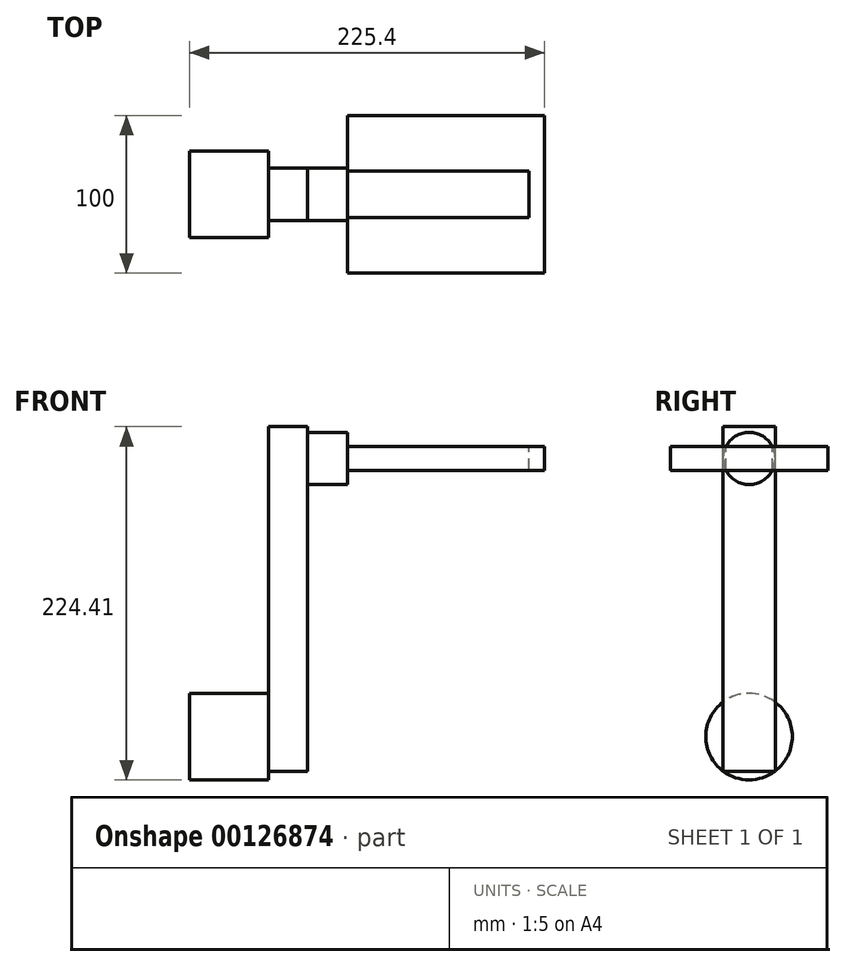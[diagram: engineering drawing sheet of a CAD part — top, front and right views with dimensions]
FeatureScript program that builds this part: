
annotation { "Feature Type Name" : "Feature", "Feature Type Description" : "" }
export const myFeature = defineFeature(function(context is Context, id is Id, definition is map)
    precondition{}
    {
        {
            var Q0;
            Q0=qCreatedBy(makeId("Right.planeOp"),FACE);
            var sketch = newSketch(context, id + "F0", { "sketchPlane" : qUnion([Q0])});
            skCircle(sketch, "E0", {"center": v(-5.47, 22.01) * mm, "radius": 27.5 * mm});
            skSolve(sketch);
        }
        {
            var Q0;
            Q0=makeQuery(id+"F0.imprint","IMPRINT",FACE,{"disambiguationData":[TD([[makeQuery(id+"F0.imprint","IMPRINT",EDGE,{"derivedFrom":sQuery(id+"F0.wireOp",EDGE,"E0")}),1.0]])]});
            extrude(context, id + "F1", {"entities" : qUnion([Q0]), "depth" : 50 * mm});
        }
        {
            var Q0;
            Q0=makeQuery(id+"F1.opExtrude","CAP_FACE",FACE,{"disambiguationData":[OSD([sQuery(id+"F0.wireOp",EDGE,"E0")])],"isStart":false});
            var sketch = newSketch(context, id + "F2", { "sketchPlane" : qUnion([Q0])});
            skLineSegment(sketch, "E1.bottom", {"start": v(-21.95, 0) * mm, "end": v(11.16, 0) * mm});
            skLineSegment(sketch, "E1.top", {"start": v(-21.95, 43.92) * mm, "end": v(11.16, 43.92) * mm});
            skLineSegment(sketch, "E1.left", {"start": v(-21.95, 0) * mm, "end": v(-21.95, 43.92) * mm});
            skLineSegment(sketch, "E1.right", {"start": v(11.16, 0) * mm, "end": v(11.16, 43.92) * mm});
            skSolve(sketch);
        }
        {
            var Q0;
            {var subQ0=sQuery(id+"F2.wireOp",EDGE,"E1.right");var subQ1=sQuery(id+"F2.wireOp",EDGE,"E1.bottom");var subQ2=makeQuery(id+"F2.imprint","INTERSECT",VERTEX,{"derivedFrom":[subQ1,subQ0]});Q0=makeQuery(id+"F2.imprint","IMPRINT",FACE,{"disambiguationData":[TD([[makeQuery(id+"F2.imprint","IMPRINT",EDGE,{"disambiguationData":[TD([[subQ2,1.0]])],"derivedFrom":subQ1}),1.0]])]});}
            var Q1;
            {var subQ1=sQuery(id+"F2.wireOp",EDGE,"E1.top");Q1=makeQuery(id+"F2.imprint","IMPRINT",FACE,{"disambiguationData":[TD([[makeQuery(id+"F2.imprint","IMPRINT",EDGE,{"derivedFrom":subQ1}),-1.0]])]});}
            extrude(context, id + "F3", {"entities" : qUnion([Q0, Q1]), "operationType" : NewBodyOperationType.ADD, "depth" : 25 * mm});
        }
        {
            var Q0;
            Q0=makeQuery(id+"F3.opExtrude","SWEPT_FACE",FACE,{"disambiguationData":[OSD([sQuery(id+"F2.wireOp",EDGE,"E1.top")])]});
            var sketch = newSketch(context, id + "F4", { "sketchPlane" : qUnion([Q0])});
            skLineSegment(sketch, "E2.bottom", {"start": v(75, 11.16) * mm, "end": v(50, 11.16) * mm});
            skLineSegment(sketch, "E2.top", {"start": v(75, -21.95) * mm, "end": v(50, -21.95) * mm});
            skLineSegment(sketch, "E2.left", {"start": v(75, 11.16) * mm, "end": v(75, -21.95) * mm});
            skLineSegment(sketch, "E2.right", {"start": v(50, 11.16) * mm, "end": v(50, -21.95) * mm});
            skSolve(sketch);
        }
        {
            var Q0;
            Q0=makeQuery(id+"F4.imprint","IMPRINT",FACE,{"disambiguationData":[TD([[makeQuery(id+"F4.imprint","IMPRINT",EDGE,{"derivedFrom":sQuery(id+"F4.wireOp",EDGE,"E2.bottom")}),1.0]])]});
            extrude(context, id + "F5", {"entities" : qUnion([Q0]), "operationType" : NewBodyOperationType.ADD, "depth" : 175 * mm});
        }
        {
            var Q0;
            Q0=makeQuery(id+"F5.boolean.opBoolean","MERGE",FACE,{"derivedFrom":[makeQuery(id+"F3.opExtrude","CAP_FACE",FACE,{"disambiguationData":[OSD([sQuery(id+"F2.wireOp",EDGE,"E1.bottom"),sQuery(id+"F2.wireOp",EDGE,"E1.top"),sQuery(id+"F2.wireOp",EDGE,"E1.left"),sQuery(id+"F2.wireOp",EDGE,"E1.right")])],"isStart":false}),makeQuery(id+"F5.opExtrude","SWEPT_FACE",FACE,{"disambiguationData":[OSD([sQuery(id+"F4.wireOp",EDGE,"E2.left")])]})]});
            var sketch = newSketch(context, id + "F6", { "sketchPlane" : qUnion([Q0])});
            skCircle(sketch, "E3", {"center": v(-5.4, 198.66) * mm, "radius": 16.56 * mm});
            skPoint(sketch, "E3.centerSnap0", {"position": v(-5.4, 218.92) * mm});
            skSolve(sketch);
        }
        {
            var Q0;
            {var subQ0=sQuery(id+"F6.wireOp",EDGE,"E3");var subQ1=sQuery(id+"F4.wireOp",EDGE,"E2.left");var subQ2=makeQuery(id+"F6.imprint","INTERSECT",VERTEX,{"derivedFrom":[makeQuery(id+"F5.boolean.opBoolean","MERGE",EDGE,{"derivedFrom":[makeQuery(id+"F3.opExtrude","CAP_EDGE",EDGE,{"disambiguationData":[OSD([sQuery(id+"F2.wireOp",EDGE,"E1.left")])],"isStart":false}),makeQuery(id+"F5.opExtrude","SWEPT_EDGE",EDGE,{"disambiguationData":[OSD([sQuery(id+"F4.wireOp",EDGE,"E2.top"),subQ1])]})]}),subQ0]});Q0=makeQuery(id+"F6.imprint","IMPRINT",FACE,{"disambiguationData":[TD([[makeQuery(id+"F6.imprint","IMPRINT",EDGE,{"disambiguationData":[TD([[subQ2,1.0]])],"derivedFrom":subQ0}),1.0]])]});}
            extrude(context, id + "F7", {"entities" : qUnion([Q0]), "operationType" : NewBodyOperationType.ADD, "depth" : 25.4 * mm});
        }
        {
            var Q0;
            Q0=makeQuery(id+"F7.opExtrude","CAP_FACE",FACE,{"disambiguationData":[OSD([sQuery(id+"F6.wireOp",EDGE,"E3")])],"isStart":false});
            var sketch = newSketch(context, id + "F8", { "sketchPlane" : qUnion([Q0])});
            skLineSegment(sketch, "E4.bottom", {"start": v(-55.4, 206.16) * mm, "end": v(44.6, 206.16) * mm});
            skLineSegment(sketch, "E4.top", {"start": v(-55.4, 191.16) * mm, "end": v(44.6, 191.16) * mm});
            skLineSegment(sketch, "E4.left", {"start": v(-55.4, 206.16) * mm, "end": v(-55.4, 191.16) * mm});
            skLineSegment(sketch, "E4.right", {"start": v(44.6, 206.16) * mm, "end": v(44.6, 191.16) * mm});
            skPoint(sketch, "E5", {"position": v(-5.4, 198.66) * mm});
            skSolve(sketch);
        }
        {
            var Q0;
            {var subQ0=sQuery(id+"F8.wireOp",EDGE,"E4.left");Q0=makeQuery(id+"F8.imprint","IMPRINT",FACE,{"disambiguationData":[TD([[makeQuery(id+"F8.imprint","IMPRINT",EDGE,{"derivedFrom":subQ0}),1.0]])]});}
            var Q1;
            {var subQ0=sQuery(id+"F8.wireOp",EDGE,"E4.right");Q1=makeQuery(id+"F8.imprint","IMPRINT",FACE,{"disambiguationData":[TD([[makeQuery(id+"F8.imprint","IMPRINT",EDGE,{"derivedFrom":subQ0}),-1.0]])]});}
            var Q2;
            {var subQ0=sQuery(id+"F8.wireOp",EDGE,"E4.bottom");var subQ1=makeQuery(id+"F7.opExtrude","CAP_EDGE",EDGE,{"disambiguationData":[OSD([sQuery(id+"F6.wireOp",EDGE,"E3")])],"isStart":false});var subQ2=makeQuery(id+"F8.imprint","INTERSECT",VERTEX,{"disambiguationData":[OD(0.0)],"derivedFrom":[subQ1,subQ0]});Q2=makeQuery(id+"F8.imprint","IMPRINT",FACE,{"disambiguationData":[TD([[makeQuery(id+"F8.imprint","IMPRINT",EDGE,{"disambiguationData":[TD([[subQ2,-1.0]])],"derivedFrom":subQ0}),-1.0]])]});}
            extrude(context, id + "F9", {"entities" : qUnion([Q0, Q1, Q2]), "operationType" : NewBodyOperationType.ADD, "depth" : 125 * mm});
        }
        {
            var Q0;
            Q0=makeQuery(id+"F9.opExtrude","SWEPT_FACE",FACE,{"disambiguationData":[OSD([sQuery(id+"F8.wireOp",EDGE,"E4.bottom")])]});
            var sketch = newSketch(context, id + "F10", { "sketchPlane" : qUnion([Q0])});
            skLineSegment(sketch, "E6.left", {"start": v(100.4, 9.37) * mm, "end": v(100.4, -20.14) * mm});
            skLineSegment(sketch, "E7.bottom", {"start": v(100.4, 9.37) * mm, "end": v(215.5, 9.37) * mm});
            skLineSegment(sketch, "E7.top", {"start": v(100.4, -20.14) * mm, "end": v(215.5, -20.14) * mm});
            skLineSegment(sketch, "E7.right", {"start": v(215.5, 9.37) * mm, "end": v(215.5, -20.14) * mm});
            skSolve(sketch);
        }
        {
            var Q0;
            Q0=makeQuery(id+"F10.imprint","IMPRINT",FACE,{"disambiguationData":[TD([[makeQuery(id+"F10.imprint","IMPRINT",EDGE,{"derivedFrom":sQuery(id+"F10.wireOp",EDGE,"E7.bottom")}),-1.0]])]});
            extrude(context, id + "F11", {"entities" : qUnion([Q0]), "operationType" : NewBodyOperationType.REMOVE, "oppositeDirection" : true, "depth" : 25.4 * mm});
        }
    });
